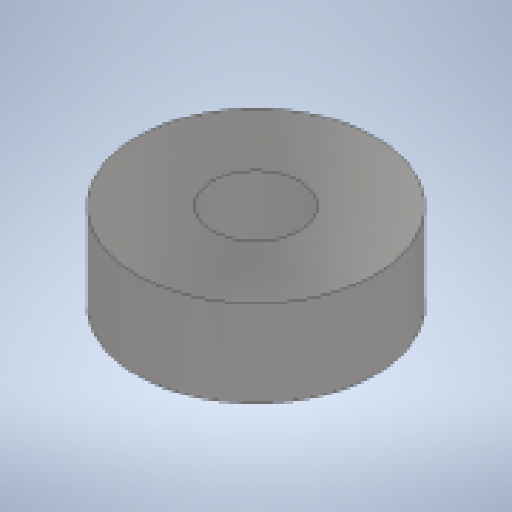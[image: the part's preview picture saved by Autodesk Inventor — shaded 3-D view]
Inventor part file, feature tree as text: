
AUTODESK INVENTOR PART (.ipt)
format: ipt  version: 2023.1 (Build 271208000, 208)  size: 137,216 bytes
history: native  units: in
note: dims shown in document units (in); Inventor stores cm internally (conversion verified against a paired STEP export)
features: extrude x1, sketch x1
ambient origin geometry x8: Origin, YZ Plane, XZ Plane, XY Plane, X Axis, Y Axis, Z Axis, Center Point
bodies: Solid1 (feature_tree)
feature tree (2):
  extrude  "Extrusion1"  Depth=0.1575in
  sketch  "Sketch1"  dims[d0=0.1575in d1=0.4331in d2=0.1575in d3=0.0in]
